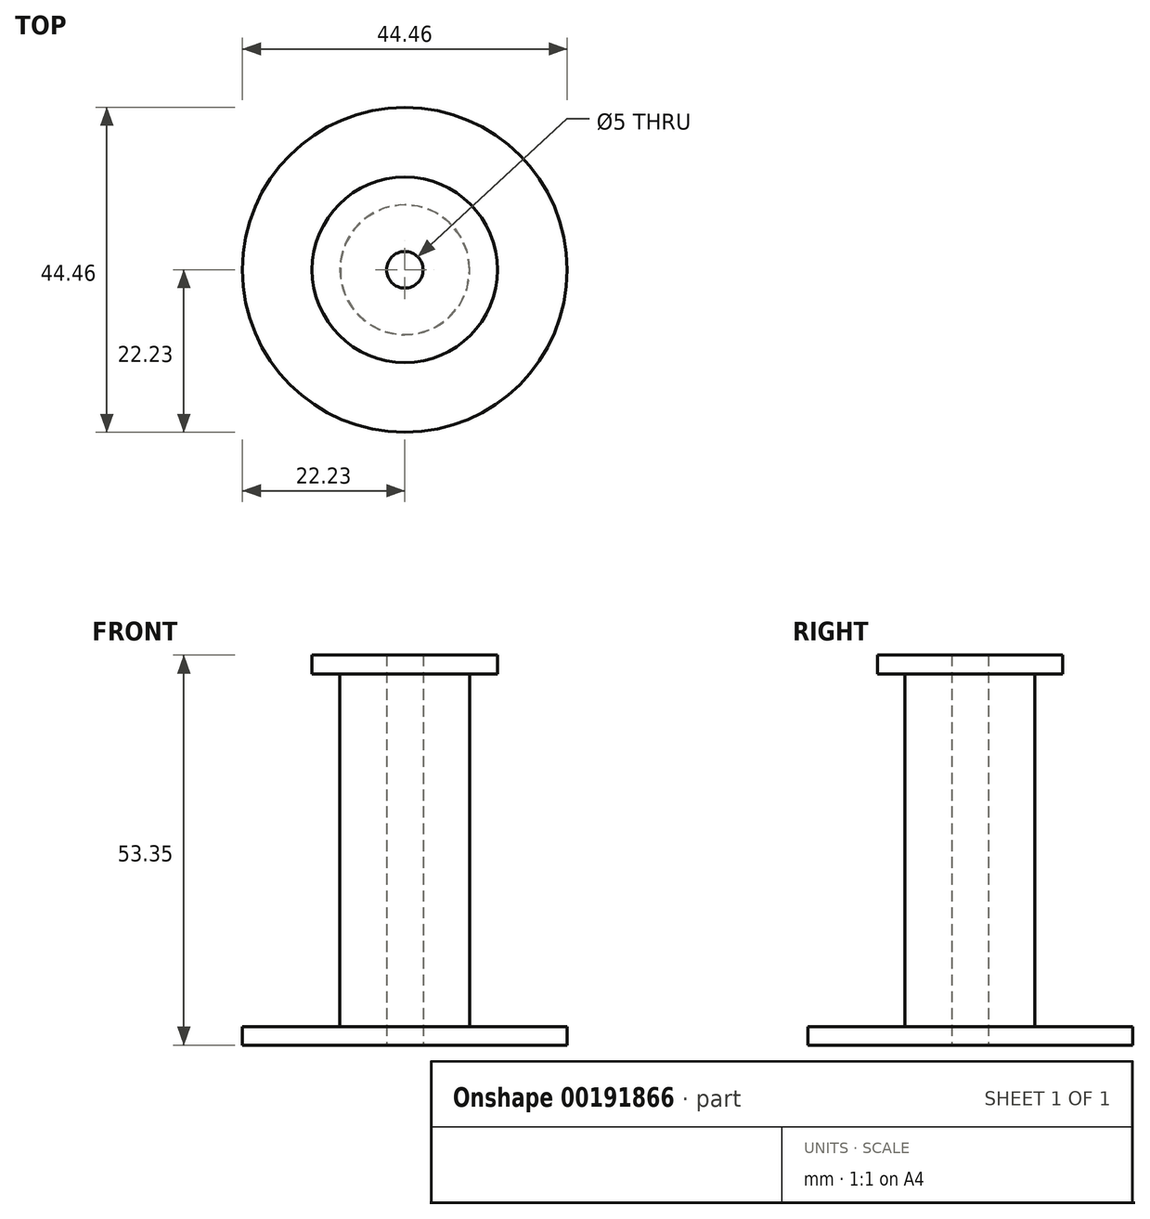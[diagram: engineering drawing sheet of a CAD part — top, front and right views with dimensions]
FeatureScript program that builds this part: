
annotation { "Feature Type Name" : "Feature", "Feature Type Description" : "" }
export const myFeature = defineFeature(function(context is Context, id is Id, definition is map)
    precondition{}
    {
        {
            var Q0;
            Q0=qCreatedBy(makeId("Top.planeOp"),FACE);
            var sketch = newSketch(context, id + "F0", { "sketchPlane" : qUnion([Q0])});
            skCircle(sketch, "E0", {"center": v(0, 0) * mm, "radius": 8.9 * mm});
            skSolve(sketch);
        }
        {
            var Q0;
            Q0=qCreatedBy(makeId("Top.planeOp"),FACE);
            var sketch = newSketch(context, id + "F1", { "sketchPlane" : qUnion([Q0])});
            skCircle(sketch, "E1", {"center": v(0, 0) * mm, "radius": 2.5 * mm});
            skSolve(sketch);
        }
        {
            var Q0;
            Q0=makeQuery(id+"F0.imprint","IMPRINT",FACE,{"disambiguationData":[TD([[makeQuery(id+"F0.imprint","IMPRINT",EDGE,{"derivedFrom":sQuery(id+"F0.wireOp",EDGE,"E0")}),1.0]])]});
            extrude(context, id + "F2", {"entities" : qUnion([Q0]), "depth" : 50.8 * mm});
        }
        {
            var Q0;
            Q0=qCreatedBy(makeId("Top.planeOp"),FACE);
            var sketch = newSketch(context, id + "F3", { "sketchPlane" : qUnion([Q0])});
            skCircle(sketch, "E2", {"center": v(0, 0) * mm, "radius": 22.23 * mm});
            skSolve(sketch);
        }
        {
            var Q0;
            Q0=makeQuery(id+"F3.imprint","IMPRINT",FACE,{"disambiguationData":[TD([[makeQuery(id+"F3.imprint","IMPRINT",EDGE,{"derivedFrom":sQuery(id+"F3.wireOp",EDGE,"E2")}),1.0]])]});
            extrude(context, id + "F4", {"entities" : qUnion([Q0]), "operationType" : NewBodyOperationType.ADD, "depth" : 2.54 * mm});
        }
        {
            var Q0;
            Q0=qCreatedBy(makeId("Front.planeOp"),FACE);
            var sketch = newSketch(context, id + "F5", { "sketchPlane" : qUnion([Q0])});
            skLineSegment(sketch, "E3", {"start": v(0, 50.8) * mm, "end": v(12.7, 50.8) * mm});
            skLineSegment(sketch, "E4", {"start": v(12.7, 50.8) * mm, "end": v(12.7, 53.35) * mm});
            skLineSegment(sketch, "E5", {"start": v(12.7, 53.35) * mm, "end": v(0, 53.35) * mm});
            skLineSegment(sketch, "E6", {"start": v(0, 53.35) * mm, "end": v(0, 50.8) * mm});
            skSolve(sketch);
        }
        {
            var Q0;
            Q0 = qSketchRegion(id + "F5", true);
            var Q1;
            Q1=sQuery(id+"F5.wireOp",EDGE,"E6");
            revolve(context, id + "F6", {"operationType" : NewBodyOperationType.ADD, "entities" : qUnion([Q0]), "axis" : qUnion([Q1]), "revolveType" : RevolveType.FULL});
        }
        {
            var Q0;
            Q0 = qSketchRegion(id + "F1", true);
            extrude(context, id + "F7", {"entities" : qUnion([Q0]), "operationType" : NewBodyOperationType.REMOVE, "endBound" : BoundingType.THROUGH_ALL, "depth" : 25.4 * mm});
        }
    });
